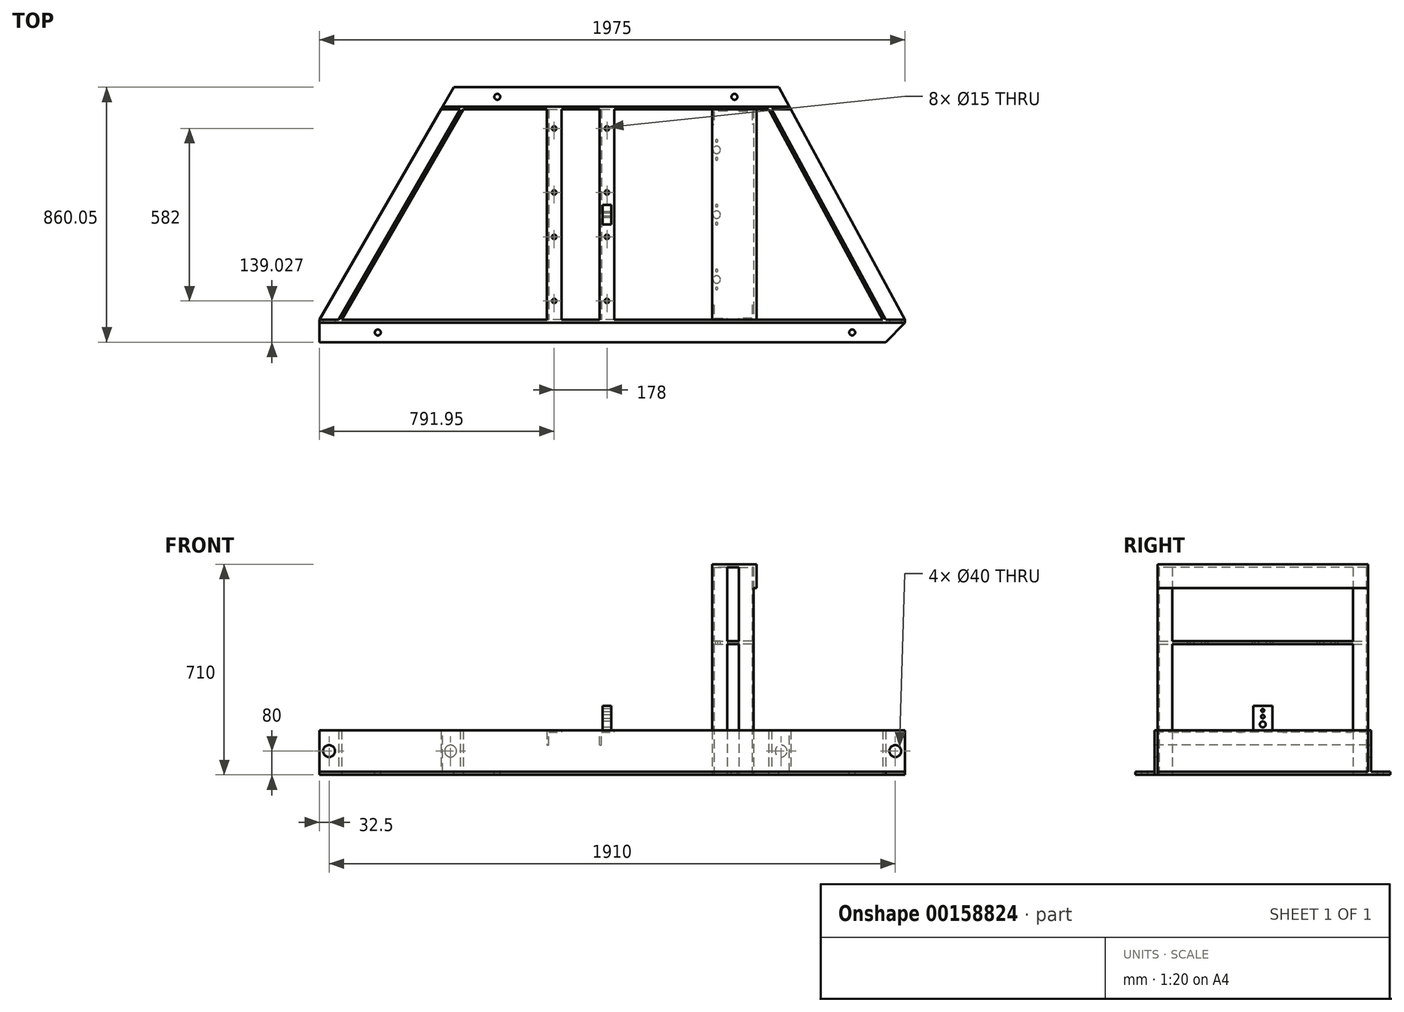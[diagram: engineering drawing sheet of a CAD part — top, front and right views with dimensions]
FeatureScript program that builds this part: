
annotation { "Feature Type Name" : "Feature", "Feature Type Description" : "" }
export const myFeature = defineFeature(function(context is Context, id is Id, definition is map)
    precondition{}
    {
        {
            var Q0;
            Q0=qCreatedBy(makeId("Right.planeOp"),FACE);
            var sketch = newSketch(context, id + "F0", { "sketchPlane" : qUnion([Q0])});
            skLineSegment(sketch, "E0.bottom", {"start": v(0, 0) * mm, "end": v(75, 0) * mm});
            skLineSegment(sketch, "E0.top", {"start": v(0, 10) * mm, "end": v(75, 10) * mm});
            skLineSegment(sketch, "E0.left", {"start": v(0, 0) * mm, "end": v(0, 10) * mm});
            skLineSegment(sketch, "E0.right", {"start": v(75, 0) * mm, "end": v(75, 10) * mm});
            skLineSegment(sketch, "E1.bottom", {"start": v(75, 0) * mm, "end": v(65, 0) * mm});
            skLineSegment(sketch, "E1.top", {"start": v(75, 150) * mm, "end": v(65, 150) * mm});
            skLineSegment(sketch, "E1.left", {"start": v(75, 0) * mm, "end": v(75, 150) * mm});
            skLineSegment(sketch, "E1.right", {"start": v(65, 0) * mm, "end": v(65, 150) * mm});
            skSolve(sketch);
        }
        {
            var Q0;
            Q0=qSketchRegion(id+"F0",true);
            extrude(context, id + "F1", {"entities" : qUnion([Q0]), "depth" : 1975 * mm});
        }
        {
            var Q0;
            Q0=qCreatedBy(makeId("Top.planeOp"),FACE);
            var sketch = newSketch(context, id + "F2", { "sketchPlane" : qUnion([Q0])});
            skLineSegment(sketch, "E2", {"start": v(0, 75) * mm, "end": v(409.95, 785.05) * mm});
            skLineSegment(sketch, "E3", {"start": v(75, 75) * mm, "end": v(484.95, 785.05) * mm});
            skLineSegment(sketch, "E4", {"start": v(409.95, 785.05) * mm, "end": v(484.95, 785.05) * mm});
            skLineSegment(sketch, "E5", {"start": v(0, 75) * mm, "end": v(75, 75) * mm});
            skSolve(sketch);
        }
        {
            var Q0;
            Q0=makeQuery(id+"F2.imprint","IMPRINT",FACE,{"disambiguationData":[TD([[makeQuery(id+"F2.imprint","IMPRINT",EDGE,{"derivedFrom":sQuery(id+"F2.wireOp",EDGE,"E2")}),-1.0]])]});
            extrude(context, id + "F3", {"entities" : qUnion([Q0]), "operationType" : NewBodyOperationType.ADD, "depth" : 10 * mm});
        }
        {
            var Q0;
            Q0=makeQuery(id+"F3.opExtrude","CAP_FACE",FACE,{"disambiguationData":[OSD([sQuery(id+"F2.wireOp",EDGE,"E2"),sQuery(id+"F2.wireOp",EDGE,"E3"),sQuery(id+"F2.wireOp",EDGE,"E4"),sQuery(id+"F2.wireOp",EDGE,"E5")])],"isStart":false});
            var sketch = newSketch(context, id + "F4", { "sketchPlane" : qUnion([Q0])});
            skLineSegment(sketch, "E6", {"start": v(484.95, 785.05) * mm, "end": v(75, 75) * mm});
            skLineSegment(sketch, "E7", {"start": v(75, 75) * mm, "end": v(65, 75) * mm});
            skLineSegment(sketch, "E8", {"start": v(65, 75) * mm, "end": v(474.95, 785.05) * mm});
            skLineSegment(sketch, "E9", {"start": v(474.95, 785.05) * mm, "end": v(484.95, 785.05) * mm});
            skSolve(sketch);
        }
        {
            var Q0;
            Q0=qSketchRegion(id+"F4",true);
            extrude(context, id + "F5", {"entities" : qUnion([Q0]), "operationType" : NewBodyOperationType.ADD, "depth" : 140 * mm});
        }
        {
            var Q0;
            Q0=qCreatedBy(makeId("Top.planeOp"),FACE);
            var sketch = newSketch(context, id + "F6", { "sketchPlane" : qUnion([Q0])});
            skLineSegment(sketch, "E10", {"start": v(409.95, 785.05) * mm, "end": v(1589.95, 785.05) * mm});
            skLineSegment(sketch, "E11", {"start": v(409.95, 785.05) * mm, "end": v(409.95, 860.05) * mm});
            skLineSegment(sketch, "E12", {"start": v(409.95, 860.05) * mm, "end": v(1589.95, 860.05) * mm});
            skLineSegment(sketch, "E13", {"start": v(1589.95, 860.05) * mm, "end": v(1589.95, 785.05) * mm});
            skSolve(sketch);
        }
        {
            var Q0;
            Q0=qSketchRegion(id+"F6",true);
            extrude(context, id + "F7", {"entities" : qUnion([Q0]), "operationType" : NewBodyOperationType.ADD, "depth" : 10 * mm});
        }
        {
            var Q0;
            Q0=makeQuery(id+"F7.boolean.opBoolean","MERGE",FACE,{"derivedFrom":[makeQuery(id+"F3.opExtrude","CAP_FACE",FACE,{"disambiguationData":[OSD([sQuery(id+"F2.wireOp",EDGE,"E2"),sQuery(id+"F2.wireOp",EDGE,"E3"),sQuery(id+"F2.wireOp",EDGE,"E4"),sQuery(id+"F2.wireOp",EDGE,"E5")])],"isStart":false}),makeQuery(id+"F7.opExtrude","CAP_FACE",FACE,{"disambiguationData":[OSD([sQuery(id+"F6.wireOp",EDGE,"E10"),sQuery(id+"F6.wireOp",EDGE,"E11"),sQuery(id+"F6.wireOp",EDGE,"E12"),sQuery(id+"F6.wireOp",EDGE,"E13")])],"isStart":false})]});
            var sketch = newSketch(context, id + "F8", { "sketchPlane" : qUnion([Q0])});
            skLineSegment(sketch, "E14", {"start": v(409.95, 785.05) * mm, "end": v(1589.95, 785.05) * mm});
            skLineSegment(sketch, "E15", {"start": v(1589.95, 785.05) * mm, "end": v(1589.95, 795.05) * mm});
            skLineSegment(sketch, "E16", {"start": v(1589.95, 795.05) * mm, "end": v(409.95, 795.05) * mm});
            skLineSegment(sketch, "E17", {"start": v(409.95, 795.05) * mm, "end": v(409.95, 785.05) * mm});
            skSolve(sketch);
        }
        {
            var Q0;
            Q0=qSketchRegion(id+"F8",true);
            extrude(context, id + "F9", {"entities" : qUnion([Q0]), "operationType" : NewBodyOperationType.ADD, "depth" : 140 * mm});
        }
        {
            var Q0;
            Q0=qCreatedBy(makeId("Top.planeOp"),FACE);
            var sketch = newSketch(context, id + "F10", { "sketchPlane" : qUnion([Q0])});
            skLineSegment(sketch, "E18", {"start": v(1589.95, 785.05) * mm, "end": v(1975, 75) * mm});
            skLineSegment(sketch, "E19", {"start": v(1975, 75) * mm, "end": v(1900, 75) * mm});
            skLineSegment(sketch, "E20", {"start": v(1900, 75) * mm, "end": v(1514.95, 785.05) * mm});
            skLineSegment(sketch, "E21", {"start": v(1514.95, 785.05) * mm, "end": v(1589.95, 785.05) * mm});
            skSolve(sketch);
        }
        {
            var Q0;
            Q0=qSketchRegion(id+"F10",true);
            extrude(context, id + "F11", {"entities" : qUnion([Q0]), "operationType" : NewBodyOperationType.ADD, "depth" : 10 * mm});
        }
        {
            var Q0;
            Q0=makeQuery(id+"F11.opExtrude","CAP_FACE",FACE,{"disambiguationData":[OSD([sQuery(id+"F10.wireOp",EDGE,"E18"),sQuery(id+"F10.wireOp",EDGE,"E19"),sQuery(id+"F10.wireOp",EDGE,"E20"),sQuery(id+"F10.wireOp",EDGE,"E21")])],"isStart":false});
            var sketch = newSketch(context, id + "F12", { "sketchPlane" : qUnion([Q0])});
            skLineSegment(sketch, "E22", {"start": v(1514.95, 785.05) * mm, "end": v(1900, 75) * mm});
            skLineSegment(sketch, "E23", {"start": v(1900, 75) * mm, "end": v(1910, 75) * mm});
            skLineSegment(sketch, "E24", {"start": v(1910, 75) * mm, "end": v(1524.95, 785.05) * mm});
            skLineSegment(sketch, "E25", {"start": v(1524.95, 785.05) * mm, "end": v(1514.95, 785.05) * mm});
            skSolve(sketch);
        }
        {
            var Q0;
            Q0=qSketchRegion(id+"F12",true);
            extrude(context, id + "F13", {"entities" : qUnion([Q0]), "operationType" : NewBodyOperationType.ADD, "depth" : 140 * mm});
        }
        {
            var Q0;
            Q0=makeQuery(id+"F1.opExtrude","SWEPT_FACE",FACE,{"disambiguationData":[OSD([sQuery(id+"F0.wireOp",EDGE,"E1.right")])]});
            var sketch = newSketch(context, id + "F14", { "sketchPlane" : qUnion([Q0])});
            skPoint(sketch, "E26", {"position": v(32.5, 80) * mm});
            skPoint(sketch, "E27", {"position": v(1942.5, 80) * mm});
            skSolve(sketch);
        }
        {
            var Q0;
            Q0=sQuery(id+"F14.wireOp",VERTEX,"E26");
            var Q1;
            Q1=sQuery(id+"F14.wireOp",VERTEX,"E27");
            var Q2;
            Q2=makeQuery(id+"F1.opExtrude","SWEPT_BODY",BODY,{"disambiguationData":[OSD([sQuery(id+"F0.wireOp",EDGE,"E0.bottom"),sQuery(id+"F0.wireOp",EDGE,"E0.top"),sQuery(id+"F0.wireOp",EDGE,"E0.left"),sQuery(id+"F0.wireOp",EDGE,"E1.bottom"),sQuery(id+"F0.wireOp",EDGE,"E1.top"),sQuery(id+"F0.wireOp",EDGE,"E1.left"),sQuery(id+"F0.wireOp",EDGE,"E1.right")])]});
            hole(context, id + "F15", {"style" : HoleStyle.SIMPLE, "endStyle" : HoleEndStyle.THROUGH, "holeDiameter" : 40 * mm, "locations" : qUnion([Q0, Q1]), "scope" : qUnion([Q2]), "isTappedThrough" : true});
        }
        {
            var Q0;
            Q0=makeQuery(id+"F9.opExtrude","SWEPT_FACE",FACE,{"disambiguationData":[OSD([sQuery(id+"F8.wireOp",EDGE,"E16")])]});
            var sketch = newSketch(context, id + "F16", { "sketchPlane" : qUnion([Q0])});
            skPoint(sketch, "E28", {"position": v(-1557.45, 80) * mm});
            skPoint(sketch, "E29", {"position": v(-442.45, 80) * mm});
            skSolve(sketch);
        }
        {
            var Q0;
            Q0=sQuery(id+"F16.wireOp",VERTEX,"E28");
            var Q1;
            Q1=sQuery(id+"F16.wireOp",VERTEX,"E29");
            var Q2;
            Q2=makeQuery(id+"F1.opExtrude","SWEPT_BODY",BODY,{"disambiguationData":[OSD([sQuery(id+"F0.wireOp",EDGE,"E0.bottom"),sQuery(id+"F0.wireOp",EDGE,"E0.top"),sQuery(id+"F0.wireOp",EDGE,"E0.left"),sQuery(id+"F0.wireOp",EDGE,"E1.bottom"),sQuery(id+"F0.wireOp",EDGE,"E1.top"),sQuery(id+"F0.wireOp",EDGE,"E1.left"),sQuery(id+"F0.wireOp",EDGE,"E1.right")])]});
            hole(context, id + "F17", {"style" : HoleStyle.SIMPLE, "endStyle" : HoleEndStyle.BLIND, "holeDiameter" : 40 * mm, "holeDepth" : 12 * mm, "locations" : qUnion([Q0, Q1]), "scope" : qUnion([Q2])});
        }
        {
            var Q0;
            Q0=makeQuery(id+"F13.boolean.opBoolean","MERGE",FACE,{"derivedFrom":[makeQuery(id+"F9.boolean.opBoolean","MERGE",FACE,{"derivedFrom":[makeQuery(id+"F5.boolean.opBoolean","MERGE",FACE,{"derivedFrom":[makeQuery(id+"F1.opExtrude","SWEPT_FACE",FACE,{"disambiguationData":[OSD([sQuery(id+"F0.wireOp",EDGE,"E1.top")])]}),makeQuery(id+"F5.opExtrude","CAP_FACE",FACE,{"disambiguationData":[OSD([sQuery(id+"F4.wireOp",EDGE,"E6"),sQuery(id+"F4.wireOp",EDGE,"E7"),sQuery(id+"F4.wireOp",EDGE,"E8"),sQuery(id+"F4.wireOp",EDGE,"E9")])],"isStart":false})]}),makeQuery(id+"F9.opExtrude","CAP_FACE",FACE,{"disambiguationData":[OSD([sQuery(id+"F8.wireOp",EDGE,"E14"),sQuery(id+"F8.wireOp",EDGE,"E15"),sQuery(id+"F8.wireOp",EDGE,"E16"),sQuery(id+"F8.wireOp",EDGE,"E17")])],"isStart":false})]}),makeQuery(id+"F13.opExtrude","CAP_FACE",FACE,{"disambiguationData":[OSD([sQuery(id+"F12.wireOp",EDGE,"E22"),sQuery(id+"F12.wireOp",EDGE,"E23"),sQuery(id+"F12.wireOp",EDGE,"E24"),sQuery(id+"F12.wireOp",EDGE,"E25")])],"isStart":false})]});
            var sketch = newSketch(context, id + "F18", { "sketchPlane" : qUnion([Q0])});
            skLineSegment(sketch, "E30.bottom", {"start": v(766.95, 65) * mm, "end": v(816.95, 65) * mm});
            skLineSegment(sketch, "E30.top", {"start": v(766.95, 795.05) * mm, "end": v(816.95, 795.05) * mm});
            skLineSegment(sketch, "E30.left", {"start": v(766.95, 65) * mm, "end": v(766.95, 795.05) * mm});
            skLineSegment(sketch, "E30.right", {"start": v(816.95, 65) * mm, "end": v(816.95, 795.05) * mm});
            skLineSegment(sketch, "E31.bottom", {"start": v(944.95, 795.05) * mm, "end": v(994.95, 795.05) * mm});
            skLineSegment(sketch, "E31.top", {"start": v(944.95, 65) * mm, "end": v(994.95, 65) * mm});
            skLineSegment(sketch, "E31.left", {"start": v(994.95, 795.05) * mm, "end": v(994.95, 65) * mm});
            skLineSegment(sketch, "E31.right", {"start": v(944.95, 795.05) * mm, "end": v(944.95, 65) * mm});
            skLineSegment(sketch, "E32", {"start": v(766.95, 430.03) * mm, "end": v(1162.6, 430.03) * mm, "construction": true});
            skPoint(sketch, "E32.endSnap0", {"position": v(766.95, 430.03) * mm});
            skCircle(sketch, "E33", {"center": v(791.95, 139.03) * mm, "radius": 7.5 * mm});
            skPoint(sketch, "E33.centerSnap0", {"position": v(791.95, 65) * mm});
            skCircle(sketch, "E34", {"center": v(791.95, 355.03) * mm, "radius": 7.5 * mm});
            skCircle(sketch, "E35.1.0.0", {"center": v(969.95, 139.03) * mm, "radius": 7.5 * mm});
            skCircle(sketch, "E35.1.0.1", {"center": v(969.95, 355.03) * mm, "radius": 7.5 * mm});
            skLineSegment(sketch, "E35.direction1", {"start": v(791.95, 139.03) * mm, "end": v(969.95, 139.03) * mm, "construction": true});
            skCircle(sketch, "E36.MirrorC", {"center": v(791.95, 505.03) * mm, "radius": 7.5 * mm});
            skCircle(sketch, "E37.MirrorC", {"center": v(791.95, 721.03) * mm, "radius": 7.5 * mm});
            skCircle(sketch, "E38.MirrorC", {"center": v(969.95, 505.03) * mm, "radius": 7.5 * mm});
            skCircle(sketch, "E39.MirrorC", {"center": v(969.95, 721.03) * mm, "radius": 7.5 * mm});
            skSolve(sketch);
        }
        {
            var Q0;
            Q0=qSketchRegion(id+"F18",true);
            extrude(context, id + "F19", {"entities" : qUnion([Q0]), "operationType" : NewBodyOperationType.ADD, "oppositeDirection" : true, "depth" : 6 * mm});
        }
        {
            var Q0;
            Q0=makeQuery(id+"F19.opExtrude","CAP_FACE",FACE,{"disambiguationData":[OSD([sQuery(id+"F18.wireOp",EDGE,"E31.bottom"),sQuery(id+"F18.wireOp",EDGE,"E31.top"),sQuery(id+"F18.wireOp",EDGE,"E31.left"),sQuery(id+"F18.wireOp",EDGE,"E31.right"),sQuery(id+"F18.wireOp",EDGE,"E35.1.0.0"),sQuery(id+"F18.wireOp",EDGE,"E35.1.0.1"),sQuery(id+"F18.wireOp",EDGE,"E38.MirrorC"),sQuery(id+"F18.wireOp",EDGE,"E39.MirrorC")])],"isStart":false});
            var sketch = newSketch(context, id + "F20", { "sketchPlane" : qUnion([Q0])});
            skLineSegment(sketch, "E40.bottom", {"start": v(944.95, -785.05) * mm, "end": v(950.95, -785.05) * mm});
            skLineSegment(sketch, "E40.top", {"start": v(944.95, -75) * mm, "end": v(950.95, -75) * mm});
            skLineSegment(sketch, "E40.left", {"start": v(944.95, -785.05) * mm, "end": v(944.95, -75) * mm});
            skLineSegment(sketch, "E40.right", {"start": v(950.95, -785.05) * mm, "end": v(950.95, -75) * mm});
            skLineSegment(sketch, "E41.1.0.0", {"start": v(766.95, -785.05) * mm, "end": v(766.95, -75) * mm});
            skLineSegment(sketch, "E41.1.0.1", {"start": v(772.95, -785.05) * mm, "end": v(772.95, -75) * mm});
            skLineSegment(sketch, "E41.1.0.2", {"start": v(766.95, -785.05) * mm, "end": v(772.95, -785.05) * mm});
            skLineSegment(sketch, "E41.1.0.3", {"start": v(766.95, -75) * mm, "end": v(772.95, -75) * mm});
            skLineSegment(sketch, "E41.direction1", {"start": v(944.95, -785.05) * mm, "end": v(766.95, -785.05) * mm, "construction": true});
            skSolve(sketch);
        }
        {
            var Q0;
            Q0=qSketchRegion(id+"F20",true);
            extrude(context, id + "F21", {"entities" : qUnion([Q0]), "operationType" : NewBodyOperationType.ADD, "depth" : 44 * mm});
        }
        {
            var Q0;
            Q0=qCreatedBy(makeId("Top.planeOp"),FACE);
            var sketch = newSketch(context, id + "F22", { "sketchPlane" : qUnion([Q0])});
            skLineSegment(sketch, "E42.bottom", {"start": v(1414.95, 785.05) * mm, "end": v(1464.95, 785.05) * mm});
            skLineSegment(sketch, "E42.top", {"start": v(1414.95, 779.05) * mm, "end": v(1464.95, 779.05) * mm});
            skLineSegment(sketch, "E42.left", {"start": v(1414.95, 785.05) * mm, "end": v(1414.95, 779.05) * mm});
            skLineSegment(sketch, "E42.right", {"start": v(1464.95, 785.05) * mm, "end": v(1464.95, 779.05) * mm});
            skLineSegment(sketch, "E43.bottom", {"start": v(1464.95, 785.05) * mm, "end": v(1458.95, 785.05) * mm});
            skLineSegment(sketch, "E43.top", {"start": v(1464.95, 735.05) * mm, "end": v(1458.95, 735.05) * mm});
            skLineSegment(sketch, "E43.left", {"start": v(1464.95, 785.05) * mm, "end": v(1464.95, 735.05) * mm});
            skLineSegment(sketch, "E43.right", {"start": v(1458.95, 785.05) * mm, "end": v(1458.95, 735.05) * mm});
            skLineSegment(sketch, "E44.bottom", {"start": v(1458.95, 125) * mm, "end": v(1464.95, 125) * mm});
            skLineSegment(sketch, "E44.top", {"start": v(1458.95, 75) * mm, "end": v(1464.95, 75) * mm});
            skLineSegment(sketch, "E44.left", {"start": v(1458.95, 125) * mm, "end": v(1458.95, 75) * mm});
            skLineSegment(sketch, "E44.right", {"start": v(1464.95, 125) * mm, "end": v(1464.95, 75) * mm});
            skLineSegment(sketch, "E45.bottom", {"start": v(1458.95, 75) * mm, "end": v(1414.95, 75) * mm});
            skLineSegment(sketch, "E45.top", {"start": v(1458.95, 81) * mm, "end": v(1414.95, 81) * mm});
            skLineSegment(sketch, "E45.left", {"start": v(1458.95, 75) * mm, "end": v(1458.95, 81) * mm});
            skLineSegment(sketch, "E45.right", {"start": v(1414.95, 75) * mm, "end": v(1414.95, 81) * mm});
            skLineSegment(sketch, "E46", {"start": v(1394.95, 829.97) * mm, "end": v(1394.95, -33.08) * mm, "construction": true});
            skLineSegment(sketch, "E47.MirrorCS", {"start": v(1324.95, 785.05) * mm, "end": v(1324.95, 735.05) * mm});
            skLineSegment(sketch, "E48.MirrorCS", {"start": v(1330.95, 785.05) * mm, "end": v(1330.95, 735.05) * mm});
            skLineSegment(sketch, "E49.MirrorCS", {"start": v(1374.95, 779.05) * mm, "end": v(1324.95, 779.05) * mm});
            skLineSegment(sketch, "E50.MirrorCS", {"start": v(1374.95, 785.05) * mm, "end": v(1324.95, 785.05) * mm});
            skLineSegment(sketch, "E51.MirrorCS", {"start": v(1324.95, 735.05) * mm, "end": v(1330.95, 735.05) * mm});
            skLineSegment(sketch, "E52.MirrorCS", {"start": v(1374.95, 785.05) * mm, "end": v(1374.95, 779.05) * mm});
            skLineSegment(sketch, "E53.MirrorCS", {"start": v(1324.95, 125) * mm, "end": v(1324.95, 75) * mm});
            skLineSegment(sketch, "E54.MirrorCS", {"start": v(1330.95, 125) * mm, "end": v(1324.95, 125) * mm});
            skLineSegment(sketch, "E55.MirrorCS", {"start": v(1330.95, 81) * mm, "end": v(1374.95, 81) * mm});
            skLineSegment(sketch, "E56.MirrorCS", {"start": v(1330.95, 75) * mm, "end": v(1374.95, 75) * mm});
            skLineSegment(sketch, "E57.MirrorCS", {"start": v(1374.95, 75) * mm, "end": v(1374.95, 81) * mm});
            skPoint(sketch, "E58.orphan", {"position": v(1330.95, 75) * mm});
            skPoint(sketch, "E59.MirrorCS.start.orphan", {"position": v(1330.95, 125) * mm});
            skLineSegment(sketch, "E60", {"start": v(1330.95, 125) * mm, "end": v(1330.95, 81) * mm});
            skLineSegment(sketch, "E61", {"start": v(1324.95, 75) * mm, "end": v(1330.95, 75) * mm});
            skSolve(sketch);
        }
        {
            var Q0;
            Q0=qSketchRegion(id+"F22",true);
            extrude(context, id + "F23", {"entities" : qUnion([Q0]), "operationType" : NewBodyOperationType.ADD, "depth" : 700 * mm});
        }
        {
            var Q0;
            Q0=makeQuery(id+"F23.opExtrude","CAP_FACE",FACE,{"disambiguationData":[OSD([sQuery(id+"F22.wireOp",EDGE,"E44.bottom"),sQuery(id+"F22.wireOp",EDGE,"E44.top"),sQuery(id+"F22.wireOp",EDGE,"E44.left"),sQuery(id+"F22.wireOp",EDGE,"E44.right"),sQuery(id+"F22.wireOp",EDGE,"E45.bottom"),sQuery(id+"F22.wireOp",EDGE,"E45.top"),sQuery(id+"F22.wireOp",EDGE,"E45.right")])],"isStart":false});
            var sketch = newSketch(context, id + "F24", { "sketchPlane" : qUnion([Q0])});
            skLineSegment(sketch, "E62.bottom", {"start": v(1324.95, 785) * mm, "end": v(1474.95, 785) * mm});
            skLineSegment(sketch, "E62.top", {"start": v(1324.95, 75) * mm, "end": v(1474.95, 75) * mm});
            skLineSegment(sketch, "E62.left", {"start": v(1324.95, 785) * mm, "end": v(1324.95, 75) * mm});
            skLineSegment(sketch, "E62.right", {"start": v(1474.95, 785) * mm, "end": v(1474.95, 75) * mm});
            skSolve(sketch);
        }
        {
            var Q0;
            Q0=qSketchRegion(id+"F24",true);
            extrude(context, id + "F25", {"entities" : qUnion([Q0]), "operationType" : NewBodyOperationType.ADD, "depth" : 10 * mm});
        }
        {
            var Q0;
            Q0=makeQuery(id+"F25.opExtrude","CAP_FACE",FACE,{"disambiguationData":[OSD([sQuery(id+"F24.wireOp",EDGE,"E62.bottom"),sQuery(id+"F24.wireOp",EDGE,"E62.top"),sQuery(id+"F24.wireOp",EDGE,"E62.left"),sQuery(id+"F24.wireOp",EDGE,"E62.right")])],"isStart":true});
            var sketch = newSketch(context, id + "F26", { "sketchPlane" : qUnion([Q0])});
            skLineSegment(sketch, "E63.bottom", {"start": v(1474.95, -75) * mm, "end": v(1464.95, -75) * mm});
            skLineSegment(sketch, "E63.top", {"start": v(1474.95, -785) * mm, "end": v(1464.95, -785) * mm});
            skLineSegment(sketch, "E63.left", {"start": v(1474.95, -75) * mm, "end": v(1474.95, -785) * mm});
            skLineSegment(sketch, "E63.right", {"start": v(1464.95, -75) * mm, "end": v(1464.95, -785) * mm});
            skSolve(sketch);
        }
        {
            var Q0;
            Q0=qSketchRegion(id+"F26",true);
            extrude(context, id + "F27", {"entities" : qUnion([Q0]), "operationType" : NewBodyOperationType.ADD, "depth" : 70 * mm});
        }
        {
            var Q0;
            Q0=makeQuery(id+"F27.boolean.opBoolean","MERGE",FACE,{"derivedFrom":[makeQuery(id+"F25.boolean.opBoolean","MERGE",FACE,{"derivedFrom":[makeQuery(id+"F23.opExtrude","SWEPT_FACE",FACE,{"disambiguationData":[OSD([sQuery(id+"F22.wireOp",EDGE,"E44.top"),sQuery(id+"F22.wireOp",EDGE,"E45.bottom")])]}),makeQuery(id+"F23.opExtrude","SWEPT_FACE",FACE,{"disambiguationData":[OSD([sQuery(id+"F22.wireOp",EDGE,"E56.MirrorCS"),sQuery(id+"F22.wireOp",EDGE,"E61")])]}),makeQuery(id+"F25.opExtrude","SWEPT_FACE",FACE,{"disambiguationData":[OSD([sQuery(id+"F24.wireOp",EDGE,"E62.top")])]})]}),makeQuery(id+"F27.opExtrude","SWEPT_FACE",FACE,{"disambiguationData":[OSD([sQuery(id+"F26.wireOp",EDGE,"E63.bottom")])]})]});
            var sketch = newSketch(context, id + "F28", { "sketchPlane" : qUnion([Q0])});
            skLineSegment(sketch, "E64.bottom", {"start": v(1324.95, 451.5) * mm, "end": v(1464.95, 451.5) * mm});
            skLineSegment(sketch, "E64.top", {"start": v(1324.95, 441.5) * mm, "end": v(1464.95, 441.5) * mm});
            skLineSegment(sketch, "E64.left", {"start": v(1324.95, 451.5) * mm, "end": v(1324.95, 441.5) * mm});
            skLineSegment(sketch, "E64.right", {"start": v(1464.95, 451.5) * mm, "end": v(1464.95, 441.5) * mm});
            skSolve(sketch);
        }
        {
            var Q0;
            Q0=qSketchRegion(id+"F28",true);
            extrude(context, id + "F29", {"entities" : qUnion([Q0]), "operationType" : NewBodyOperationType.ADD, "oppositeDirection" : true, "depth" : 710 * mm});
        }
        {
            var Q0;
            Q0=makeQuery(id+"F29.opExtrude","SWEPT_FACE",FACE,{"disambiguationData":[OSD([sQuery(id+"F28.wireOp",EDGE,"E64.bottom")])]});
            var sketch = newSketch(context, id + "F30", { "sketchPlane" : qUnion([Q0])});
            skPoint(sketch, "E65", {"position": v(1430.8, 482) * mm});
            skPoint(sketch, "E66", {"position": v(1376.8, 482) * mm});
            skPoint(sketch, "E67", {"position": v(1430.8, 378) * mm});
            skPoint(sketch, "E68", {"position": v(1376.8, 378) * mm});
            skPoint(sketch, "E69", {"position": v(1339.95, 679.05) * mm});
            skPoint(sketch, "E70", {"position": v(1339.95, 618.45) * mm});
            skPoint(sketch, "E71", {"position": v(1339.95, 241.6) * mm});
            skPoint(sketch, "E72", {"position": v(1339.95, 181) * mm});
            skCircle(sketch, "E73", {"center": v(1339.95, 211.3) * mm, "radius": 12.5 * mm});
            skCircle(sketch, "E74", {"center": v(1339.95, 648.75) * mm, "radius": 12.5 * mm});
            skPoint(sketch, "E75", {"position": v(1339.95, 399.7) * mm});
            skPoint(sketch, "E76", {"position": v(1339.95, 460.3) * mm});
            skCircle(sketch, "E77", {"center": v(1339.95, 430) * mm, "radius": 12.5 * mm});
            skSolve(sketch);
        }
        {
            var Q0;
            Q0=sQuery(id+"F30.wireOp",VERTEX,"E70");
            var Q1;
            Q1=sQuery(id+"F30.wireOp",VERTEX,"E69");
            var Q2;
            Q2=sQuery(id+"F30.wireOp",VERTEX,"E71");
            var Q3;
            Q3=sQuery(id+"F30.wireOp",VERTEX,"E72");
            var Q4;
            Q4=sQuery(id+"F30.wireOp",VERTEX,"E75");
            var Q5;
            Q5=sQuery(id+"F30.wireOp",VERTEX,"E76");
            var Q6;
            Q6=makeQuery(id+"F1.opExtrude","SWEPT_BODY",BODY,{"disambiguationData":[OSD([sQuery(id+"F0.wireOp",EDGE,"E0.bottom"),sQuery(id+"F0.wireOp",EDGE,"E0.top"),sQuery(id+"F0.wireOp",EDGE,"E0.left"),sQuery(id+"F0.wireOp",EDGE,"E1.bottom"),sQuery(id+"F0.wireOp",EDGE,"E1.top"),sQuery(id+"F0.wireOp",EDGE,"E1.left"),sQuery(id+"F0.wireOp",EDGE,"E1.right")])]});
            hole(context, id + "F31", {"style" : HoleStyle.SIMPLE, "endStyle" : HoleEndStyle.BLIND, "standardTappedOrClearance" : lookupTablePath({ "standard" : "ISO", "fit" : "Normal", "size" : "M8", "type" : "Clearance" }), "standardBlindInLast" : lookupTablePath({ "fit" : "Standard", "standard" : "ISO", "size" : "M8", "type" : "Clearance" }), "holeDiameter" : 8.8 * mm, "holeDepth" : 20 * mm, "locations" : qUnion([Q0, Q1, Q2, Q3, Q4, Q5]), "scope" : qUnion([Q6])});
        }
        {
            var Q0;
            Q0=qSketchRegion(id+"F30",true);
            extrude(context, id + "F32", {"entities" : qUnion([Q0]), "operationType" : NewBodyOperationType.REMOVE, "oppositeDirection" : true, "depth" : 25 * mm});
        }
        {
            var Q0;
            {var subQ0=sQuery(id+"F6.wireOp",EDGE,"E13");var subQ1=sQuery(id+"F6.wireOp",EDGE,"E12");var subQ2=sQuery(id+"F6.wireOp",EDGE,"E11");Q0=makeQuery(id+"F9.boolean.opBoolean","SPLIT",FACE,{"disambiguationData":[TD([makeQuery(id+"F7.opExtrude","SWEPT_FACE",FACE,{"disambiguationData":[OSD([subQ1])]})])],"derivedFrom":makeQuery(id+"F7.boolean.opBoolean","MERGE",FACE,{"derivedFrom":[makeQuery(id+"F3.opExtrude","CAP_FACE",FACE,{"disambiguationData":[OSD([sQuery(id+"F2.wireOp",EDGE,"E2"),sQuery(id+"F2.wireOp",EDGE,"E3"),sQuery(id+"F2.wireOp",EDGE,"E4"),sQuery(id+"F2.wireOp",EDGE,"E5")])],"isStart":false}),makeQuery(id+"F7.opExtrude","CAP_FACE",FACE,{"disambiguationData":[OSD([sQuery(id+"F6.wireOp",EDGE,"E10"),subQ2,subQ1,subQ0])],"isStart":false})]})});}
            var sketch = newSketch(context, id + "F33", { "sketchPlane" : qUnion([Q0])});
            skPoint(sketch, "E78", {"position": v(599.95, 827.55) * mm});
            skPoint(sketch, "E79", {"position": v(1399.95, 827.55) * mm});
            skPoint(sketch, "E80", {"position": v(1797, 32.5) * mm});
            skPoint(sketch, "E81", {"position": v(197, 32.5) * mm});
            skSolve(sketch);
        }
        {
            var Q0;
            Q0=sQuery(id+"F33.wireOp",VERTEX,"E81");
            var Q1;
            Q1=sQuery(id+"F33.wireOp",VERTEX,"E80");
            var Q2;
            Q2=sQuery(id+"F33.wireOp",VERTEX,"E79");
            var Q3;
            Q3=sQuery(id+"F33.wireOp",VERTEX,"E78");
            var Q4;
            Q4=makeQuery(id+"F1.opExtrude","SWEPT_BODY",BODY,{"disambiguationData":[OSD([sQuery(id+"F0.wireOp",EDGE,"E0.bottom"),sQuery(id+"F0.wireOp",EDGE,"E0.top"),sQuery(id+"F0.wireOp",EDGE,"E0.left"),sQuery(id+"F0.wireOp",EDGE,"E1.bottom"),sQuery(id+"F0.wireOp",EDGE,"E1.top"),sQuery(id+"F0.wireOp",EDGE,"E1.left"),sQuery(id+"F0.wireOp",EDGE,"E1.right")])]});
            hole(context, id + "F34", {"style" : HoleStyle.SIMPLE, "endStyle" : HoleEndStyle.THROUGH, "holeDiameter" : 20 * mm, "locations" : qUnion([Q0, Q1, Q2, Q3]), "scope" : qUnion([Q4]), "isTappedThrough" : true});
        }
        {
            var Q0;
            {var subQ0=sQuery(id+"F6.wireOp",EDGE,"E13");var subQ1=sQuery(id+"F6.wireOp",EDGE,"E12");var subQ2=sQuery(id+"F6.wireOp",EDGE,"E11");Q0=makeQuery(id+"F9.boolean.opBoolean","SPLIT",FACE,{"disambiguationData":[TD([makeQuery(id+"F7.opExtrude","SWEPT_FACE",FACE,{"disambiguationData":[OSD([subQ1])]})])],"derivedFrom":makeQuery(id+"F7.boolean.opBoolean","MERGE",FACE,{"derivedFrom":[makeQuery(id+"F3.opExtrude","CAP_FACE",FACE,{"disambiguationData":[OSD([sQuery(id+"F2.wireOp",EDGE,"E2"),sQuery(id+"F2.wireOp",EDGE,"E3"),sQuery(id+"F2.wireOp",EDGE,"E4"),sQuery(id+"F2.wireOp",EDGE,"E5")])],"isStart":false}),makeQuery(id+"F7.opExtrude","CAP_FACE",FACE,{"disambiguationData":[OSD([sQuery(id+"F6.wireOp",EDGE,"E10"),subQ2,subQ1,subQ0])],"isStart":false})]})});}
            var sketch = newSketch(context, id + "F35", { "sketchPlane" : qUnion([Q0])});
            skLineSegment(sketch, "E82", {"start": v(1910, 0) * mm, "end": v(1975, 65) * mm});
            skLineSegment(sketch, "E83", {"start": v(1975, 65) * mm, "end": v(1975, 0) * mm});
            skLineSegment(sketch, "E84", {"start": v(1975, 0) * mm, "end": v(1910, 0) * mm});
            skLineSegment(sketch, "E85.0", {"start": v(0, 75) * mm, "end": v(409.95, 785.05) * mm});
            skLineSegment(sketch, "E86", {"start": v(409.95, 785.05) * mm, "end": v(453.25, 860.05) * mm});
            skLineSegment(sketch, "E87", {"start": v(409.95, 785.05) * mm, "end": v(409.95, 860.05) * mm});
            skLineSegment(sketch, "E88", {"start": v(409.95, 860.05) * mm, "end": v(453.25, 860.05) * mm});
            skLineSegment(sketch, "E89.0", {"start": v(1589.95, 785.05) * mm, "end": v(1975, 75) * mm});
            skLineSegment(sketch, "E90", {"start": v(1589.95, 785.05) * mm, "end": v(1549.28, 860.05) * mm});
            skLineSegment(sketch, "E91", {"start": v(1549.28, 860.05) * mm, "end": v(1589.95, 860.05) * mm});
            skLineSegment(sketch, "E92", {"start": v(1589.95, 860.05) * mm, "end": v(1589.95, 785.05) * mm});
            skSolve(sketch);
        }
        {
            var Q0;
            Q0=qSketchRegion(id+"F35",true);
            extrude(context, id + "F36", {"entities" : qUnion([Q0]), "operationType" : NewBodyOperationType.REMOVE, "oppositeDirection" : true, "depth" : 25 * mm, "hasSecondDirection" : true, "secondDirectionOppositeDirection" : false, "secondDirectionDepth" : 227 * mm});
        }
        {
            var Q0;
            Q0=makeQuery(id+"F19.boolean.opBoolean","MERGE",FACE,{"derivedFrom":[makeQuery(id+"F13.boolean.opBoolean","MERGE",FACE,{"derivedFrom":[makeQuery(id+"F9.boolean.opBoolean","MERGE",FACE,{"derivedFrom":[makeQuery(id+"F5.boolean.opBoolean","MERGE",FACE,{"derivedFrom":[makeQuery(id+"F1.opExtrude","SWEPT_FACE",FACE,{"disambiguationData":[OSD([sQuery(id+"F0.wireOp",EDGE,"E1.top")])]}),makeQuery(id+"F5.opExtrude","CAP_FACE",FACE,{"disambiguationData":[OSD([sQuery(id+"F4.wireOp",EDGE,"E6"),sQuery(id+"F4.wireOp",EDGE,"E7"),sQuery(id+"F4.wireOp",EDGE,"E8"),sQuery(id+"F4.wireOp",EDGE,"E9")])],"isStart":false})]}),makeQuery(id+"F9.opExtrude","CAP_FACE",FACE,{"disambiguationData":[OSD([sQuery(id+"F8.wireOp",EDGE,"E14"),sQuery(id+"F8.wireOp",EDGE,"E15"),sQuery(id+"F8.wireOp",EDGE,"E16"),sQuery(id+"F8.wireOp",EDGE,"E17")])],"isStart":false})]}),makeQuery(id+"F13.opExtrude","CAP_FACE",FACE,{"disambiguationData":[OSD([sQuery(id+"F12.wireOp",EDGE,"E22"),sQuery(id+"F12.wireOp",EDGE,"E23"),sQuery(id+"F12.wireOp",EDGE,"E24"),sQuery(id+"F12.wireOp",EDGE,"E25")])],"isStart":false})]}),makeQuery(id+"F19.opExtrude","CAP_FACE",FACE,{"disambiguationData":[OSD([sQuery(id+"F18.wireOp",EDGE,"E30.bottom"),sQuery(id+"F18.wireOp",EDGE,"E30.top"),sQuery(id+"F18.wireOp",EDGE,"E30.left"),sQuery(id+"F18.wireOp",EDGE,"E30.right"),sQuery(id+"F18.wireOp",EDGE,"E33"),sQuery(id+"F18.wireOp",EDGE,"E34"),sQuery(id+"F18.wireOp",EDGE,"E37.MirrorC"),sQuery(id+"F18.wireOp",EDGE,"E36.MirrorC")])],"isStart":true}),makeQuery(id+"F19.opExtrude","CAP_FACE",FACE,{"disambiguationData":[OSD([sQuery(id+"F18.wireOp",EDGE,"E31.bottom"),sQuery(id+"F18.wireOp",EDGE,"E31.top"),sQuery(id+"F18.wireOp",EDGE,"E31.left"),sQuery(id+"F18.wireOp",EDGE,"E31.right"),sQuery(id+"F18.wireOp",EDGE,"E35.1.0.0"),sQuery(id+"F18.wireOp",EDGE,"E35.1.0.1"),sQuery(id+"F18.wireOp",EDGE,"E38.MirrorC"),sQuery(id+"F18.wireOp",EDGE,"E39.MirrorC")])],"isStart":true})]});
            var sketch = newSketch(context, id + "F37", { "sketchPlane" : qUnion([Q0])});
            skLineSegment(sketch, "E93.bottom", {"start": v(954.95, 397.53) * mm, "end": v(984.95, 397.53) * mm});
            skLineSegment(sketch, "E93.top", {"start": v(954.95, 462.53) * mm, "end": v(984.95, 462.53) * mm});
            skLineSegment(sketch, "E93.left", {"start": v(954.95, 397.53) * mm, "end": v(954.95, 462.53) * mm});
            skLineSegment(sketch, "E93.right", {"start": v(984.95, 397.53) * mm, "end": v(984.95, 462.53) * mm});
            skPoint(sketch, "E93.middle", {"position": v(969.95, 430.03) * mm});
            skPoint(sketch, "E93.middle.positionSnap0", {"position": v(944.95, 430.03) * mm});
            skPoint(sketch, "E93.centerSnap0", {"position": v(944.95, 430.03) * mm});
            skSolve(sketch);
        }
        {
            var Q0;
            Q0 = qSketchRegion(id + "F37", true);
            extrude(context, id + "F38", {"entities" : qUnion([Q0]), "operationType" : NewBodyOperationType.ADD, "depth" : 82 * mm});
        }
        {
            var Q0;
            Q0=makeQuery(id+"F38.opExtrude","SWEPT_FACE",FACE,{"disambiguationData":[OSD([sQuery(id+"F37.wireOp",EDGE,"E93.left")])]});
            var sketch = newSketch(context, id + "F39", { "sketchPlane" : qUnion([Q0])});
            skCircle(sketch, "E94", {"center": v(-430.03, 170) * mm, "radius": 10 * mm});
            skPoint(sketch, "E94.centerSnap0", {"position": v(-430.03, 232) * mm});
            skCircle(sketch, "E95", {"center": v(-430.03, 196) * mm, "radius": 6 * mm});
            skCircle(sketch, "E96", {"center": v(-430.03, 217) * mm, "radius": 5 * mm});
            skSolve(sketch);
        }
        {
            var Q0;
            Q0 = qSketchRegion(id + "F39", true);
            extrude(context, id + "F40", {"entities" : qUnion([Q0]), "operationType" : NewBodyOperationType.REMOVE, "oppositeDirection" : true, "depth" : 30 * mm});
        }
    });
